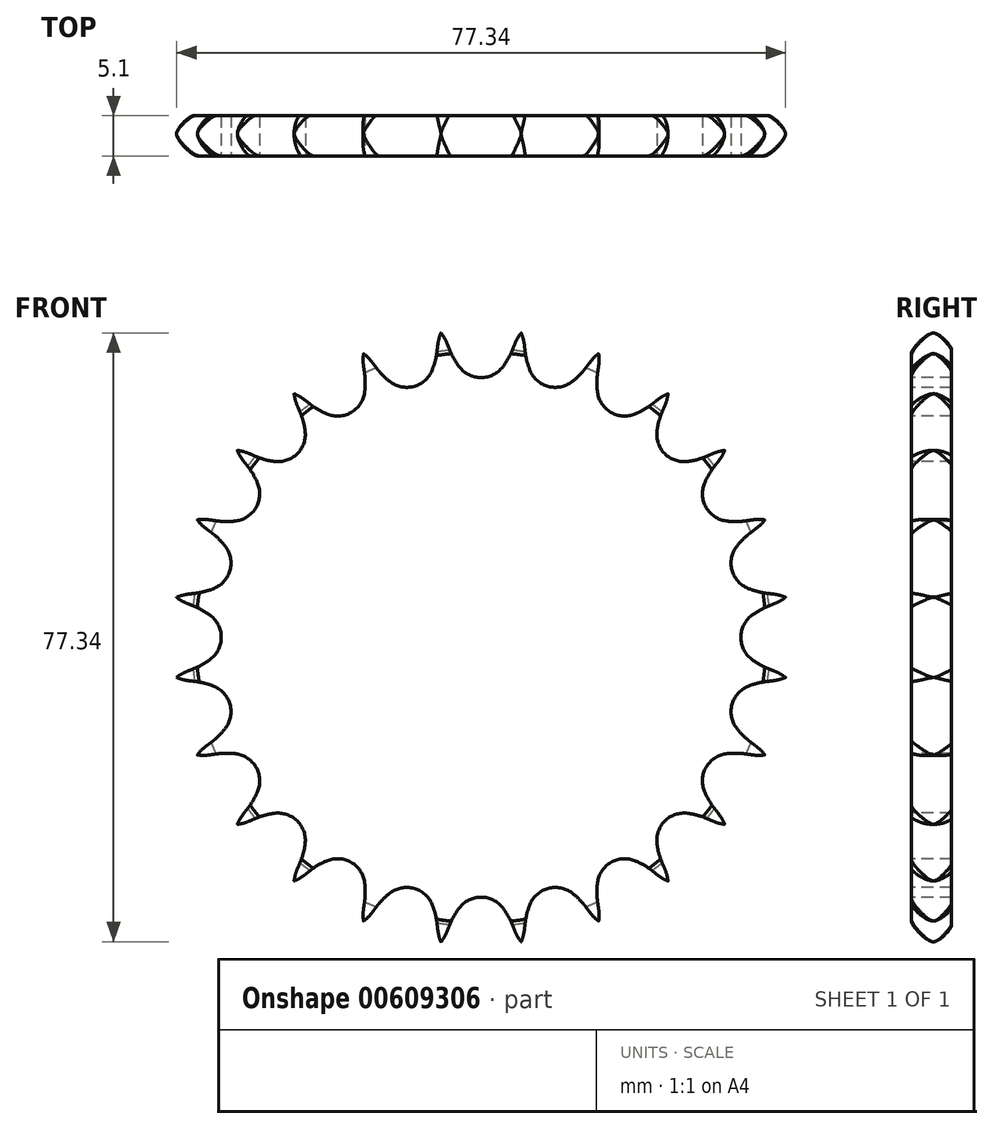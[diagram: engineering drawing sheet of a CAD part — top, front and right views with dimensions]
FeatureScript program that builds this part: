
annotation { "Feature Type Name" : "Feature", "Feature Type Description" : "" }
export const myFeature = defineFeature(function(context is Context, id is Id, definition is map)
    precondition{}
    {
        {
            var Q0;
            Q0=qCreatedBy(makeId("Right.planeOp"),FACE);
            var sketch = newSketch(context, id + "F0", { "sketchPlane" : qUnion([Q0])});
            skLineSegment(sketch, "E0", {"start": v(0, 0) * mm, "end": v(5.1, 0) * mm, "construction": true});
            skLineSegment(sketch, "E1", {"start": v(0, 39) * mm, "end": v(5.1, 39) * mm});
            skLineSegment(sketch, "E2", {"start": v(5.1, 39) * mm, "end": v(5.1, 30) * mm});
            skLineSegment(sketch, "E3", {"start": v(5.1, 30) * mm, "end": v(5.1, 30) * mm});
            skLineSegment(sketch, "E4", {"start": v(5.1, 30) * mm, "end": v(5.1, 0) * mm});
            skLineSegment(sketch, "E5", {"start": v(0, 0) * mm, "end": v(0, 39) * mm});
            skLineSegment(sketch, "E6.0.MirrorCS", {"start": v(0, -39) * mm, "end": v(5.1, -39) * mm});
            skLineSegment(sketch, "E6.1.MirrorCS", {"start": v(5.1, -39) * mm, "end": v(5.1, -30) * mm});
            skLineSegment(sketch, "E6.3.MirrorCS", {"start": v(5.1, -30) * mm, "end": v(5.1, 0) * mm});
            skLineSegment(sketch, "E6.4.MirrorCS", {"start": v(5.1, -30) * mm, "end": v(5.1, -30) * mm});
            skLineSegment(sketch, "E6.5.MirrorCS", {"start": v(0, 0) * mm, "end": v(0, -39) * mm});
            skLineSegment(sketch, "E7", {"start": v(0, 0) * mm, "end": v(5.1, 0) * mm});
            skLineSegment(sketch, "E8", {"start": v(5.1, 30) * mm, "end": v(0, 30) * mm, "construction": true});
            skLineSegment(sketch, "E9", {"start": v(5.1, -30) * mm, "end": v(0, -30) * mm, "construction": true});
            skSolve(sketch);
        }
        {
            var Q0;
            Q0=makeQuery(id+"F0.imprint","IMPRINT",FACE,{"disambiguationData":[TD([[makeQuery(id+"F0.imprint","IMPRINT",EDGE,{"derivedFrom":sQuery(id+"F0.wireOp",EDGE,"E1")}),-1.0]])]});
            var Q1;
            Q1=sQuery(id+"F0.wireOp",EDGE,"E0");
            revolve(context, id + "F1", {"entities" : qUnion([Q0]), "axis" : qUnion([Q1]), "revolveType" : RevolveType.FULL});
        }
        {
            var Q0;
            Q0=makeQuery(id+"F1.opRevolve","SWEPT_EDGE",EDGE,{"disambiguationData":[OSD([sQuery(id+"F0.wireOp",EDGE,"E1"),sQuery(id+"F0.wireOp",EDGE,"E5")])]});
            fillet(context, id + "F2", {"entities" : qUnion([Q0]), "radius" : 2.75 * mm, "tangentPropagation" : true, "rho" : 0.2, "crossSection" : FilletCrossSection.CONIC, "allowEdgeOverflow" : false});
        }
        {
            var Q0;
            Q0=makeQuery(id+"F1.opRevolve","SWEPT_EDGE",EDGE,{"disambiguationData":[OSD([sQuery(id+"F0.wireOp",EDGE,"E1"),sQuery(id+"F0.wireOp",EDGE,"E2")])]});
            fillet(context, id + "F3", {"entities" : qUnion([Q0]), "radius" : 2.25 * mm, "tangentPropagation" : true, "rho" : 0.2, "crossSection" : FilletCrossSection.CONIC, "allowEdgeOverflow" : false});
        }
        {
            var Q0;
            Q0=qCreatedBy(makeId("Front.planeOp"),FACE);
            var sketch = newSketch(context, id + "F4", { "sketchPlane" : qUnion([Q0])});
            skPoint(sketch, "E10.0", {"position": v(0, 0) * mm});
            skLineSegment(sketch, "E11", {"start": v(0, 0) * mm, "end": v(0, 36.49) * mm, "construction": true});
            skLineSegment(sketch, "E12", {"start": v(0, 36.49) * mm, "end": v(75.89, 36.49) * mm, "construction": true});
            skLineSegment(sketch, "E13", {"start": v(0, 0) * mm, "end": v(-5.1, 38.69) * mm, "construction": true});
            skArc(sketch, "E14", {"start": v(-2.76, 34.37) * mm, "mid": v(12.15, 44.27) * mm, "end": v(-3.97, 36.5) * mm, "construction": true});
            skLineSegment(sketch, "E15", {"start": v(0, 0) * mm, "end": v(15.68, 0) * mm, "construction": true});
            skArc(sketch, "E16", {"start": v(-5.1, 38.69) * mm, "mid": v(-14.39, 32.43) * mm, "end": v(-4.3, 37.32) * mm, "construction": true});
            skLineSegment(sketch, "E17", {"start": v(0.64, 24.97) * mm, "end": v(-4.3, 37.32) * mm, "construction": true});
            skArc(sketch, "E18", {"start": v(2.76, 34.37) * mm, "mid": v(0, 39.97) * mm, "end": v(-2.76, 34.37) * mm, "construction": true});
            skArc(sketch, "E19.0.MirrorCS", {"start": v(3.97, 36.5) * mm, "mid": v(3.44, 35.39) * mm, "end": v(2.76, 34.37) * mm});
            skLineSegment(sketch, "E20.0.MirrorCS", {"start": v(3.97, 36.5) * mm, "end": v(4.3, 37.32) * mm});
            skArc(sketch, "E21", {"start": v(-2.76, 34.37) * mm, "mid": v(0, 33) * mm, "end": v(2.76, 34.37) * mm});
            skLineSegment(sketch, "E22", {"start": v(0, 36.49) * mm, "end": v(4.35, 39.83) * mm, "construction": true});
            skLineSegment(sketch, "E23", {"start": v(4.35, 39.83) * mm, "end": v(-3.97, 36.5) * mm, "construction": true});
            skLineSegment(sketch, "E24", {"start": v(-3.97, 36.5) * mm, "end": v(-4.3, 37.32) * mm});
            skArc(sketch, "E25", {"start": v(-4.3, 37.32) * mm, "mid": v(-4.65, 38.03) * mm, "end": v(-5.1, 38.69) * mm});
            skArc(sketch, "E26", {"start": v(-3.97, 36.5) * mm, "mid": v(-3.44, 35.39) * mm, "end": v(-2.76, 34.37) * mm});
            skArc(sketch, "E27.0.MirrorCS", {"start": v(4.3, 37.32) * mm, "mid": v(4.65, 38.03) * mm, "end": v(5.1, 38.69) * mm});
            skCircle(sketch, "E28", {"center": v(0, 0) * mm, "radius": 36.49 * mm, "construction": true});
            skArc(sketch, "E29.1.0", {"start": v(-13.82, 34.93) * mm, "mid": v(-14.34, 35.53) * mm, "end": v(-14.93, 36.05) * mm});
            skLineSegment(sketch, "E29.1.1", {"start": v(-13.28, 34.22) * mm, "end": v(-13.82, 34.93) * mm});
            skArc(sketch, "E29.1.2", {"start": v(-13.28, 34.22) * mm, "mid": v(-12.48, 33.29) * mm, "end": v(-11.56, 32.48) * mm});
            skArc(sketch, "E29.1.3", {"start": v(-11.56, 32.48) * mm, "mid": v(-8.54, 31.88) * mm, "end": v(-6.22, 33.9) * mm});
            skArc(sketch, "E29.1.4", {"start": v(-5.6, 36.28) * mm, "mid": v(-5.83, 35.07) * mm, "end": v(-6.22, 33.9) * mm});
            skLineSegment(sketch, "E29.1.5", {"start": v(-5.6, 36.28) * mm, "end": v(-5.5, 37.16) * mm});
            skArc(sketch, "E29.1.6", {"start": v(-5.5, 37.16) * mm, "mid": v(-5.35, 37.94) * mm, "end": v(-5.1, 38.69) * mm});
            skArc(sketch, "E29.2.0", {"start": v(-22.4, 30.17) * mm, "mid": v(-23.05, 30.61) * mm, "end": v(-23.76, 30.96) * mm});
            skLineSegment(sketch, "E29.2.1", {"start": v(-21.69, 29.61) * mm, "end": v(-22.4, 30.17) * mm});
            skArc(sketch, "E29.2.2", {"start": v(-21.69, 29.61) * mm, "mid": v(-20.67, 28.92) * mm, "end": v(-19.58, 28.38) * mm});
            skArc(sketch, "E29.2.3", {"start": v(-19.58, 28.38) * mm, "mid": v(-16.5, 28.58) * mm, "end": v(-14.79, 31.14) * mm});
            skArc(sketch, "E29.2.4", {"start": v(-14.8, 33.59) * mm, "mid": v(-14.71, 32.37) * mm, "end": v(-14.79, 31.14) * mm});
            skLineSegment(sketch, "E29.2.5", {"start": v(-14.8, 33.59) * mm, "end": v(-14.93, 34.47) * mm});
            skArc(sketch, "E29.2.6", {"start": v(-14.93, 34.47) * mm, "mid": v(-14.99, 35.26) * mm, "end": v(-14.93, 36.05) * mm});
            skArc(sketch, "E29.3.0", {"start": v(-29.44, 23.34) * mm, "mid": v(-30.18, 23.6) * mm, "end": v(-30.96, 23.76) * mm});
            skLineSegment(sketch, "E29.3.1", {"start": v(-28.61, 23) * mm, "end": v(-29.44, 23.34) * mm});
            skArc(sketch, "E29.3.2", {"start": v(-28.61, 23) * mm, "mid": v(-27.46, 22.59) * mm, "end": v(-26.25, 22.35) * mm});
            skArc(sketch, "E29.3.3", {"start": v(-26.25, 22.35) * mm, "mid": v(-23.34, 23.34) * mm, "end": v(-22.35, 26.25) * mm});
            skArc(sketch, "E29.3.4", {"start": v(-23, 28.61) * mm, "mid": v(-22.59, 27.46) * mm, "end": v(-22.35, 26.25) * mm});
            skLineSegment(sketch, "E29.3.5", {"start": v(-23, 28.61) * mm, "end": v(-23.34, 29.44) * mm});
            skArc(sketch, "E29.3.6", {"start": v(-23.34, 29.44) * mm, "mid": v(-23.6, 30.18) * mm, "end": v(-23.76, 30.96) * mm});
            skArc(sketch, "E29.4.0", {"start": v(-34.47, 14.93) * mm, "mid": v(-35.26, 14.99) * mm, "end": v(-36.05, 14.93) * mm});
            skLineSegment(sketch, "E29.4.1", {"start": v(-33.59, 14.8) * mm, "end": v(-34.47, 14.93) * mm});
            skArc(sketch, "E29.4.2", {"start": v(-33.59, 14.8) * mm, "mid": v(-32.37, 14.71) * mm, "end": v(-31.14, 14.79) * mm});
            skArc(sketch, "E29.4.3", {"start": v(-31.14, 14.79) * mm, "mid": v(-28.58, 16.5) * mm, "end": v(-28.38, 19.58) * mm});
            skArc(sketch, "E29.4.4", {"start": v(-29.61, 21.69) * mm, "mid": v(-28.92, 20.67) * mm, "end": v(-28.38, 19.58) * mm});
            skLineSegment(sketch, "E29.4.5", {"start": v(-29.61, 21.69) * mm, "end": v(-30.17, 22.4) * mm});
            skArc(sketch, "E29.4.6", {"start": v(-30.17, 22.4) * mm, "mid": v(-30.61, 23.05) * mm, "end": v(-30.96, 23.76) * mm});
            skArc(sketch, "E29.5.0", {"start": v(-37.16, 5.5) * mm, "mid": v(-37.94, 5.35) * mm, "end": v(-38.69, 5.1) * mm});
            skLineSegment(sketch, "E29.5.1", {"start": v(-36.28, 5.6) * mm, "end": v(-37.16, 5.5) * mm});
            skArc(sketch, "E29.5.2", {"start": v(-36.28, 5.6) * mm, "mid": v(-35.07, 5.83) * mm, "end": v(-33.9, 6.22) * mm});
            skArc(sketch, "E29.5.3", {"start": v(-33.9, 6.22) * mm, "mid": v(-31.88, 8.54) * mm, "end": v(-32.48, 11.56) * mm});
            skArc(sketch, "E29.5.4", {"start": v(-34.22, 13.28) * mm, "mid": v(-33.29, 12.48) * mm, "end": v(-32.48, 11.56) * mm});
            skLineSegment(sketch, "E29.5.5", {"start": v(-34.22, 13.28) * mm, "end": v(-34.93, 13.82) * mm});
            skArc(sketch, "E29.5.6", {"start": v(-34.93, 13.82) * mm, "mid": v(-35.53, 14.34) * mm, "end": v(-36.05, 14.93) * mm});
            skArc(sketch, "E29.6.0", {"start": v(-37.32, -4.3) * mm, "mid": v(-38.03, -4.65) * mm, "end": v(-38.69, -5.1) * mm});
            skLineSegment(sketch, "E29.6.1", {"start": v(-36.5, -3.97) * mm, "end": v(-37.32, -4.3) * mm});
            skArc(sketch, "E29.6.2", {"start": v(-36.5, -3.97) * mm, "mid": v(-35.39, -3.44) * mm, "end": v(-34.37, -2.76) * mm});
            skArc(sketch, "E29.6.3", {"start": v(-34.37, -2.76) * mm, "mid": v(-33, 0) * mm, "end": v(-34.37, 2.76) * mm});
            skArc(sketch, "E29.6.4", {"start": v(-36.5, 3.97) * mm, "mid": v(-35.39, 3.44) * mm, "end": v(-34.37, 2.76) * mm});
            skLineSegment(sketch, "E29.6.5", {"start": v(-36.5, 3.97) * mm, "end": v(-37.32, 4.3) * mm});
            skArc(sketch, "E29.6.6", {"start": v(-37.32, 4.3) * mm, "mid": v(-38.03, 4.65) * mm, "end": v(-38.69, 5.1) * mm});
            skArc(sketch, "E29.7.0", {"start": v(-34.93, -13.82) * mm, "mid": v(-35.53, -14.34) * mm, "end": v(-36.05, -14.93) * mm});
            skLineSegment(sketch, "E29.7.1", {"start": v(-34.22, -13.28) * mm, "end": v(-34.93, -13.82) * mm});
            skArc(sketch, "E29.7.2", {"start": v(-34.22, -13.28) * mm, "mid": v(-33.29, -12.48) * mm, "end": v(-32.48, -11.56) * mm});
            skArc(sketch, "E29.7.3", {"start": v(-32.48, -11.56) * mm, "mid": v(-31.88, -8.54) * mm, "end": v(-33.9, -6.22) * mm});
            skArc(sketch, "E29.7.4", {"start": v(-36.28, -5.6) * mm, "mid": v(-35.07, -5.83) * mm, "end": v(-33.9, -6.22) * mm});
            skLineSegment(sketch, "E29.7.5", {"start": v(-36.28, -5.6) * mm, "end": v(-37.16, -5.5) * mm});
            skArc(sketch, "E29.7.6", {"start": v(-37.16, -5.5) * mm, "mid": v(-37.94, -5.35) * mm, "end": v(-38.69, -5.1) * mm});
            skArc(sketch, "E29.8.0", {"start": v(-30.17, -22.4) * mm, "mid": v(-30.61, -23.05) * mm, "end": v(-30.96, -23.76) * mm});
            skLineSegment(sketch, "E29.8.1", {"start": v(-29.61, -21.69) * mm, "end": v(-30.17, -22.4) * mm});
            skArc(sketch, "E29.8.2", {"start": v(-29.61, -21.69) * mm, "mid": v(-28.92, -20.67) * mm, "end": v(-28.38, -19.58) * mm});
            skArc(sketch, "E29.8.3", {"start": v(-28.38, -19.58) * mm, "mid": v(-28.58, -16.5) * mm, "end": v(-31.14, -14.79) * mm});
            skArc(sketch, "E29.8.4", {"start": v(-33.59, -14.8) * mm, "mid": v(-32.37, -14.71) * mm, "end": v(-31.14, -14.79) * mm});
            skLineSegment(sketch, "E29.8.5", {"start": v(-33.59, -14.8) * mm, "end": v(-34.47, -14.93) * mm});
            skArc(sketch, "E29.8.6", {"start": v(-34.47, -14.93) * mm, "mid": v(-35.26, -14.99) * mm, "end": v(-36.05, -14.93) * mm});
            skArc(sketch, "E29.9.0", {"start": v(-23.34, -29.44) * mm, "mid": v(-23.6, -30.18) * mm, "end": v(-23.76, -30.96) * mm});
            skLineSegment(sketch, "E29.9.1", {"start": v(-23, -28.61) * mm, "end": v(-23.34, -29.44) * mm});
            skArc(sketch, "E29.9.2", {"start": v(-23, -28.61) * mm, "mid": v(-22.59, -27.46) * mm, "end": v(-22.35, -26.25) * mm});
            skArc(sketch, "E29.9.3", {"start": v(-22.35, -26.25) * mm, "mid": v(-23.34, -23.34) * mm, "end": v(-26.25, -22.35) * mm});
            skArc(sketch, "E29.9.4", {"start": v(-28.61, -23) * mm, "mid": v(-27.46, -22.59) * mm, "end": v(-26.25, -22.35) * mm});
            skLineSegment(sketch, "E29.9.5", {"start": v(-28.61, -23) * mm, "end": v(-29.44, -23.34) * mm});
            skArc(sketch, "E29.9.6", {"start": v(-29.44, -23.34) * mm, "mid": v(-30.18, -23.6) * mm, "end": v(-30.96, -23.76) * mm});
            skArc(sketch, "E29.10.0", {"start": v(-14.93, -34.47) * mm, "mid": v(-14.99, -35.26) * mm, "end": v(-14.93, -36.05) * mm});
            skLineSegment(sketch, "E29.10.1", {"start": v(-14.8, -33.59) * mm, "end": v(-14.93, -34.47) * mm});
            skArc(sketch, "E29.10.2", {"start": v(-14.8, -33.59) * mm, "mid": v(-14.71, -32.37) * mm, "end": v(-14.79, -31.14) * mm});
            skArc(sketch, "E29.10.3", {"start": v(-14.79, -31.14) * mm, "mid": v(-16.5, -28.58) * mm, "end": v(-19.58, -28.38) * mm});
            skArc(sketch, "E29.10.4", {"start": v(-21.69, -29.61) * mm, "mid": v(-20.67, -28.92) * mm, "end": v(-19.58, -28.38) * mm});
            skLineSegment(sketch, "E29.10.5", {"start": v(-21.69, -29.61) * mm, "end": v(-22.4, -30.17) * mm});
            skArc(sketch, "E29.10.6", {"start": v(-22.4, -30.17) * mm, "mid": v(-23.05, -30.61) * mm, "end": v(-23.76, -30.96) * mm});
            skArc(sketch, "E29.11.0", {"start": v(-5.5, -37.16) * mm, "mid": v(-5.35, -37.94) * mm, "end": v(-5.1, -38.69) * mm});
            skLineSegment(sketch, "E29.11.1", {"start": v(-5.6, -36.28) * mm, "end": v(-5.5, -37.16) * mm});
            skArc(sketch, "E29.11.2", {"start": v(-5.6, -36.28) * mm, "mid": v(-5.83, -35.07) * mm, "end": v(-6.22, -33.9) * mm});
            skArc(sketch, "E29.11.3", {"start": v(-6.22, -33.9) * mm, "mid": v(-8.54, -31.88) * mm, "end": v(-11.56, -32.48) * mm});
            skArc(sketch, "E29.11.4", {"start": v(-13.28, -34.22) * mm, "mid": v(-12.48, -33.29) * mm, "end": v(-11.56, -32.48) * mm});
            skLineSegment(sketch, "E29.11.5", {"start": v(-13.28, -34.22) * mm, "end": v(-13.82, -34.93) * mm});
            skArc(sketch, "E29.11.6", {"start": v(-13.82, -34.93) * mm, "mid": v(-14.34, -35.53) * mm, "end": v(-14.93, -36.05) * mm});
            skArc(sketch, "E29.12.0", {"start": v(4.3, -37.32) * mm, "mid": v(4.65, -38.03) * mm, "end": v(5.1, -38.69) * mm});
            skLineSegment(sketch, "E29.12.1", {"start": v(3.97, -36.5) * mm, "end": v(4.3, -37.32) * mm});
            skArc(sketch, "E29.12.2", {"start": v(3.97, -36.5) * mm, "mid": v(3.44, -35.39) * mm, "end": v(2.76, -34.37) * mm});
            skArc(sketch, "E29.12.3", {"start": v(2.76, -34.37) * mm, "mid": v(0, -33) * mm, "end": v(-2.76, -34.37) * mm});
            skArc(sketch, "E29.12.4", {"start": v(-3.97, -36.5) * mm, "mid": v(-3.44, -35.39) * mm, "end": v(-2.76, -34.37) * mm});
            skLineSegment(sketch, "E29.12.5", {"start": v(-3.97, -36.5) * mm, "end": v(-4.3, -37.32) * mm});
            skArc(sketch, "E29.12.6", {"start": v(-4.3, -37.32) * mm, "mid": v(-4.65, -38.03) * mm, "end": v(-5.1, -38.69) * mm});
            skArc(sketch, "E29.13.0", {"start": v(13.82, -34.93) * mm, "mid": v(14.34, -35.53) * mm, "end": v(14.93, -36.05) * mm});
            skLineSegment(sketch, "E29.13.1", {"start": v(13.28, -34.22) * mm, "end": v(13.82, -34.93) * mm});
            skArc(sketch, "E29.13.2", {"start": v(13.28, -34.22) * mm, "mid": v(12.48, -33.29) * mm, "end": v(11.56, -32.48) * mm});
            skArc(sketch, "E29.13.3", {"start": v(11.56, -32.48) * mm, "mid": v(8.54, -31.88) * mm, "end": v(6.22, -33.9) * mm});
            skArc(sketch, "E29.13.4", {"start": v(5.6, -36.28) * mm, "mid": v(5.83, -35.07) * mm, "end": v(6.22, -33.9) * mm});
            skLineSegment(sketch, "E29.13.5", {"start": v(5.6, -36.28) * mm, "end": v(5.5, -37.16) * mm});
            skArc(sketch, "E29.13.6", {"start": v(5.5, -37.16) * mm, "mid": v(5.35, -37.94) * mm, "end": v(5.1, -38.69) * mm});
            skArc(sketch, "E29.14.0", {"start": v(22.4, -30.17) * mm, "mid": v(23.05, -30.61) * mm, "end": v(23.76, -30.96) * mm});
            skLineSegment(sketch, "E29.14.1", {"start": v(21.69, -29.61) * mm, "end": v(22.4, -30.17) * mm});
            skArc(sketch, "E29.14.2", {"start": v(21.69, -29.61) * mm, "mid": v(20.67, -28.92) * mm, "end": v(19.58, -28.38) * mm});
            skArc(sketch, "E29.14.3", {"start": v(19.58, -28.38) * mm, "mid": v(16.5, -28.58) * mm, "end": v(14.79, -31.14) * mm});
            skArc(sketch, "E29.14.4", {"start": v(14.8, -33.59) * mm, "mid": v(14.71, -32.37) * mm, "end": v(14.79, -31.14) * mm});
            skLineSegment(sketch, "E29.14.5", {"start": v(14.8, -33.59) * mm, "end": v(14.93, -34.47) * mm});
            skArc(sketch, "E29.14.6", {"start": v(14.93, -34.47) * mm, "mid": v(14.99, -35.26) * mm, "end": v(14.93, -36.05) * mm});
            skArc(sketch, "E29.15.0", {"start": v(29.44, -23.34) * mm, "mid": v(30.18, -23.6) * mm, "end": v(30.96, -23.76) * mm});
            skLineSegment(sketch, "E29.15.1", {"start": v(28.61, -23) * mm, "end": v(29.44, -23.34) * mm});
            skArc(sketch, "E29.15.2", {"start": v(28.61, -23) * mm, "mid": v(27.46, -22.59) * mm, "end": v(26.25, -22.35) * mm});
            skArc(sketch, "E29.15.3", {"start": v(26.25, -22.35) * mm, "mid": v(23.34, -23.34) * mm, "end": v(22.35, -26.25) * mm});
            skArc(sketch, "E29.15.4", {"start": v(23, -28.61) * mm, "mid": v(22.59, -27.46) * mm, "end": v(22.35, -26.25) * mm});
            skLineSegment(sketch, "E29.15.5", {"start": v(23, -28.61) * mm, "end": v(23.34, -29.44) * mm});
            skArc(sketch, "E29.15.6", {"start": v(23.34, -29.44) * mm, "mid": v(23.6, -30.18) * mm, "end": v(23.76, -30.96) * mm});
            skArc(sketch, "E29.16.0", {"start": v(34.47, -14.93) * mm, "mid": v(35.26, -14.99) * mm, "end": v(36.05, -14.93) * mm});
            skLineSegment(sketch, "E29.16.1", {"start": v(33.59, -14.8) * mm, "end": v(34.47, -14.93) * mm});
            skArc(sketch, "E29.16.2", {"start": v(33.59, -14.8) * mm, "mid": v(32.37, -14.71) * mm, "end": v(31.14, -14.79) * mm});
            skArc(sketch, "E29.16.3", {"start": v(31.14, -14.79) * mm, "mid": v(28.58, -16.5) * mm, "end": v(28.38, -19.58) * mm});
            skArc(sketch, "E29.16.4", {"start": v(29.61, -21.69) * mm, "mid": v(28.92, -20.67) * mm, "end": v(28.38, -19.58) * mm});
            skLineSegment(sketch, "E29.16.5", {"start": v(29.61, -21.69) * mm, "end": v(30.17, -22.4) * mm});
            skArc(sketch, "E29.16.6", {"start": v(30.17, -22.4) * mm, "mid": v(30.61, -23.05) * mm, "end": v(30.96, -23.76) * mm});
            skArc(sketch, "E29.17.0", {"start": v(37.16, -5.5) * mm, "mid": v(37.94, -5.35) * mm, "end": v(38.69, -5.1) * mm});
            skLineSegment(sketch, "E29.17.1", {"start": v(36.28, -5.6) * mm, "end": v(37.16, -5.5) * mm});
            skArc(sketch, "E29.17.2", {"start": v(36.28, -5.6) * mm, "mid": v(35.07, -5.83) * mm, "end": v(33.9, -6.22) * mm});
            skArc(sketch, "E29.17.3", {"start": v(33.9, -6.22) * mm, "mid": v(31.88, -8.54) * mm, "end": v(32.48, -11.56) * mm});
            skArc(sketch, "E29.17.4", {"start": v(34.22, -13.28) * mm, "mid": v(33.29, -12.48) * mm, "end": v(32.48, -11.56) * mm});
            skLineSegment(sketch, "E29.17.5", {"start": v(34.22, -13.28) * mm, "end": v(34.93, -13.82) * mm});
            skArc(sketch, "E29.17.6", {"start": v(34.93, -13.82) * mm, "mid": v(35.53, -14.34) * mm, "end": v(36.05, -14.93) * mm});
            skArc(sketch, "E29.18.0", {"start": v(37.32, 4.3) * mm, "mid": v(38.03, 4.65) * mm, "end": v(38.69, 5.1) * mm});
            skLineSegment(sketch, "E29.18.1", {"start": v(36.5, 3.97) * mm, "end": v(37.32, 4.3) * mm});
            skArc(sketch, "E29.18.2", {"start": v(36.5, 3.97) * mm, "mid": v(35.39, 3.44) * mm, "end": v(34.37, 2.76) * mm});
            skArc(sketch, "E29.18.3", {"start": v(34.37, 2.76) * mm, "mid": v(33, 0) * mm, "end": v(34.37, -2.76) * mm});
            skArc(sketch, "E29.18.4", {"start": v(36.5, -3.97) * mm, "mid": v(35.39, -3.44) * mm, "end": v(34.37, -2.76) * mm});
            skLineSegment(sketch, "E29.18.5", {"start": v(36.5, -3.97) * mm, "end": v(37.32, -4.3) * mm});
            skArc(sketch, "E29.18.6", {"start": v(37.32, -4.3) * mm, "mid": v(38.03, -4.65) * mm, "end": v(38.69, -5.1) * mm});
            skArc(sketch, "E29.19.0", {"start": v(34.93, 13.82) * mm, "mid": v(35.53, 14.34) * mm, "end": v(36.05, 14.93) * mm});
            skLineSegment(sketch, "E29.19.1", {"start": v(34.22, 13.28) * mm, "end": v(34.93, 13.82) * mm});
            skArc(sketch, "E29.19.2", {"start": v(34.22, 13.28) * mm, "mid": v(33.29, 12.48) * mm, "end": v(32.48, 11.56) * mm});
            skArc(sketch, "E29.19.3", {"start": v(32.48, 11.56) * mm, "mid": v(31.88, 8.54) * mm, "end": v(33.9, 6.22) * mm});
            skArc(sketch, "E29.19.4", {"start": v(36.28, 5.6) * mm, "mid": v(35.07, 5.83) * mm, "end": v(33.9, 6.22) * mm});
            skLineSegment(sketch, "E29.19.5", {"start": v(36.28, 5.6) * mm, "end": v(37.16, 5.5) * mm});
            skArc(sketch, "E29.19.6", {"start": v(37.16, 5.5) * mm, "mid": v(37.94, 5.35) * mm, "end": v(38.69, 5.1) * mm});
            skArc(sketch, "E29.20.0", {"start": v(30.17, 22.4) * mm, "mid": v(30.61, 23.05) * mm, "end": v(30.96, 23.76) * mm});
            skLineSegment(sketch, "E29.20.1", {"start": v(29.61, 21.69) * mm, "end": v(30.17, 22.4) * mm});
            skArc(sketch, "E29.20.2", {"start": v(29.61, 21.69) * mm, "mid": v(28.92, 20.67) * mm, "end": v(28.38, 19.58) * mm});
            skArc(sketch, "E29.20.3", {"start": v(28.38, 19.58) * mm, "mid": v(28.58, 16.5) * mm, "end": v(31.14, 14.79) * mm});
            skArc(sketch, "E29.20.4", {"start": v(33.59, 14.8) * mm, "mid": v(32.37, 14.71) * mm, "end": v(31.14, 14.79) * mm});
            skLineSegment(sketch, "E29.20.5", {"start": v(33.59, 14.8) * mm, "end": v(34.47, 14.93) * mm});
            skArc(sketch, "E29.20.6", {"start": v(34.47, 14.93) * mm, "mid": v(35.26, 14.99) * mm, "end": v(36.05, 14.93) * mm});
            skArc(sketch, "E29.21.0", {"start": v(23.34, 29.44) * mm, "mid": v(23.6, 30.18) * mm, "end": v(23.76, 30.96) * mm});
            skLineSegment(sketch, "E29.21.1", {"start": v(23, 28.61) * mm, "end": v(23.34, 29.44) * mm});
            skArc(sketch, "E29.21.2", {"start": v(23, 28.61) * mm, "mid": v(22.59, 27.46) * mm, "end": v(22.35, 26.25) * mm});
            skArc(sketch, "E29.21.3", {"start": v(22.35, 26.25) * mm, "mid": v(23.34, 23.34) * mm, "end": v(26.25, 22.35) * mm});
            skArc(sketch, "E29.21.4", {"start": v(28.61, 23) * mm, "mid": v(27.46, 22.59) * mm, "end": v(26.25, 22.35) * mm});
            skLineSegment(sketch, "E29.21.5", {"start": v(28.61, 23) * mm, "end": v(29.44, 23.34) * mm});
            skArc(sketch, "E29.21.6", {"start": v(29.44, 23.34) * mm, "mid": v(30.18, 23.6) * mm, "end": v(30.96, 23.76) * mm});
            skArc(sketch, "E29.22.0", {"start": v(14.93, 34.47) * mm, "mid": v(14.99, 35.26) * mm, "end": v(14.93, 36.05) * mm});
            skLineSegment(sketch, "E29.22.1", {"start": v(14.8, 33.59) * mm, "end": v(14.93, 34.47) * mm});
            skArc(sketch, "E29.22.2", {"start": v(14.8, 33.59) * mm, "mid": v(14.71, 32.37) * mm, "end": v(14.79, 31.14) * mm});
            skArc(sketch, "E29.22.3", {"start": v(14.79, 31.14) * mm, "mid": v(16.5, 28.58) * mm, "end": v(19.58, 28.38) * mm});
            skArc(sketch, "E29.22.4", {"start": v(21.69, 29.61) * mm, "mid": v(20.67, 28.92) * mm, "end": v(19.58, 28.38) * mm});
            skLineSegment(sketch, "E29.22.5", {"start": v(21.69, 29.61) * mm, "end": v(22.4, 30.17) * mm});
            skArc(sketch, "E29.22.6", {"start": v(22.4, 30.17) * mm, "mid": v(23.05, 30.61) * mm, "end": v(23.76, 30.96) * mm});
            skArc(sketch, "E29.23.0", {"start": v(5.5, 37.16) * mm, "mid": v(5.35, 37.94) * mm, "end": v(5.1, 38.69) * mm});
            skLineSegment(sketch, "E29.23.1", {"start": v(5.6, 36.28) * mm, "end": v(5.5, 37.16) * mm});
            skArc(sketch, "E29.23.2", {"start": v(5.6, 36.28) * mm, "mid": v(5.83, 35.07) * mm, "end": v(6.22, 33.9) * mm});
            skArc(sketch, "E29.23.3", {"start": v(6.22, 33.9) * mm, "mid": v(8.54, 31.88) * mm, "end": v(11.56, 32.48) * mm});
            skArc(sketch, "E29.23.4", {"start": v(13.28, 34.22) * mm, "mid": v(12.48, 33.29) * mm, "end": v(11.56, 32.48) * mm});
            skLineSegment(sketch, "E29.23.5", {"start": v(13.28, 34.22) * mm, "end": v(13.82, 34.93) * mm});
            skArc(sketch, "E29.23.6", {"start": v(13.82, 34.93) * mm, "mid": v(14.34, 35.53) * mm, "end": v(14.93, 36.05) * mm});
            skSolve(sketch);
        }
        {
            var Q0;
            Q0=qSketchRegion(id+"F4",true);
            extrude(context, id + "F5", {"entities" : qUnion([Q0]), "operationType" : NewBodyOperationType.INTERSECT, "endBound" : BoundingType.THROUGH_ALL, "oppositeDirection" : true, "depth" : 25.4 * mm});
        }
    });
